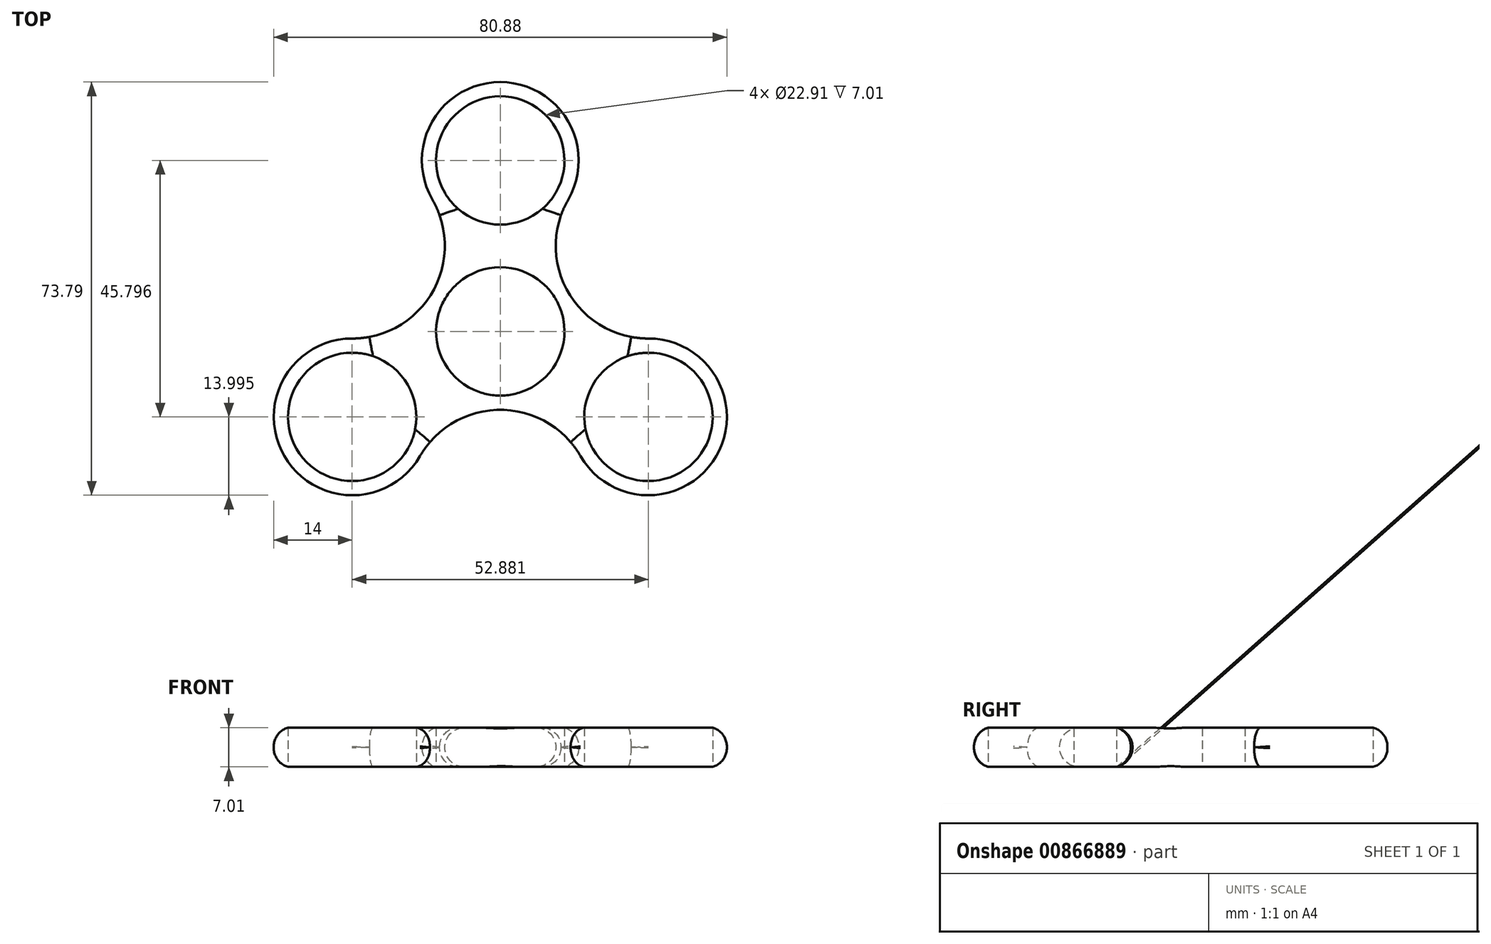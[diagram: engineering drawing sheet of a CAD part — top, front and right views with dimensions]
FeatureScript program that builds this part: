
annotation { "Feature Type Name" : "Feature", "Feature Type Description" : "" }
export const myFeature = defineFeature(function(context is Context, id is Id, definition is map)
    precondition{}
    {
        {
            var Q0;
            Q0=qCreatedBy(makeId("Top.planeOp"),FACE);
            var sketch = newSketch(context, id + "F0", { "sketchPlane" : qUnion([Q0])});
            skCircle(sketch, "E0", {"center": v(0, 0) * mm, "radius": 11.46 * mm});
            skCircle(sketch, "E1", {"center": v(0, 0) * mm, "radius": 14 * mm});
            skCircle(sketch, "E2", {"center": v(0, 30.53) * mm, "radius": 11.46 * mm});
            skCircle(sketch, "E3", {"center": v(0, 30.53) * mm, "radius": 14 * mm});
            skCircle(sketch, "E4.1.0", {"center": v(-26.44, -15.27) * mm, "radius": 11.46 * mm});
            skCircle(sketch, "E4.1.1", {"center": v(-26.44, -15.27) * mm, "radius": 14 * mm});
            skCircle(sketch, "E4.2.0", {"center": v(26.44, -15.27) * mm, "radius": 11.46 * mm});
            skCircle(sketch, "E4.2.1", {"center": v(26.44, -15.27) * mm, "radius": 14 * mm});
            skCircle(sketch, "E5", {"center": v(-26.44, 15.27) * mm, "radius": 16.54 * mm});
            skCircle(sketch, "E6.1.0", {"center": v(0, -30.53) * mm, "radius": 16.54 * mm});
            skCircle(sketch, "E6.2.0", {"center": v(26.44, 15.27) * mm, "radius": 16.54 * mm});
            skSolve(sketch);
        }
        {
            var Q0;
            Q0=makeQuery(id+"F0.imprint","IMPRINT",FACE,{"disambiguationData":[TD([[makeQuery(id+"F0.imprint","IMPRINT",EDGE,{"derivedFrom":sQuery(id+"F0.wireOp",EDGE,"E2")}),-1.0]])]});
            var Q1;
            Q1=makeQuery(id+"F0.imprint","IMPRINT",FACE,{"disambiguationData":[TD([[makeQuery(id+"F0.imprint","IMPRINT",EDGE,{"derivedFrom":sQuery(id+"F0.wireOp",EDGE,"E4.1.0")}),-1.0]])]});
            var Q2;
            Q2=makeQuery(id+"F0.imprint","IMPRINT",FACE,{"disambiguationData":[TD([[makeQuery(id+"F0.imprint","IMPRINT",EDGE,{"derivedFrom":sQuery(id+"F0.wireOp",EDGE,"E4.2.0")}),-1.0]])]});
            var Q3;
            {var subQ0=sQuery(id+"F0.wireOp",EDGE,"E5");var subQ1=sQuery(id+"F0.wireOp",EDGE,"E1");var subQ2=makeQuery(id+"F0.imprint","INTERSECT",VERTEX,{"derivedFrom":[subQ1,subQ0]});Q3=makeQuery(id+"F0.imprint","IMPRINT",FACE,{"disambiguationData":[TD([[makeQuery(id+"F0.imprint","IMPRINT",EDGE,{"disambiguationData":[TD([[subQ2,1.0]])],"derivedFrom":subQ1}),-1.0]])]});}
            var Q4;
            {var subQ0=sQuery(id+"F0.wireOp",EDGE,"E5");var subQ1=sQuery(id+"F0.wireOp",EDGE,"E1");var subQ2=makeQuery(id+"F0.imprint","INTERSECT",VERTEX,{"derivedFrom":[subQ1,subQ0]});Q4=makeQuery(id+"F0.imprint","IMPRINT",FACE,{"disambiguationData":[TD([[makeQuery(id+"F0.imprint","IMPRINT",EDGE,{"disambiguationData":[TD([[subQ2,-1.0]])],"derivedFrom":subQ1}),-1.0]])]});}
            var Q5;
            {var subQ0=sQuery(id+"F0.wireOp",EDGE,"E6.2.0");var subQ1=sQuery(id+"F0.wireOp",EDGE,"E1");var subQ2=makeQuery(id+"F0.imprint","INTERSECT",VERTEX,{"derivedFrom":[subQ1,subQ0]});Q5=makeQuery(id+"F0.imprint","IMPRINT",FACE,{"disambiguationData":[TD([[makeQuery(id+"F0.imprint","IMPRINT",EDGE,{"disambiguationData":[TD([[subQ2,1.0]])],"derivedFrom":subQ1}),-1.0]])]});}
            var Q6;
            Q6=makeQuery(id+"F0.imprint","IMPRINT",FACE,{"disambiguationData":[TD([[makeQuery(id+"F0.imprint","IMPRINT",EDGE,{"derivedFrom":sQuery(id+"F0.wireOp",EDGE,"E0")}),-1.0]])]});
            extrude(context, id + "F1", {"entities" : qUnion([Q0, Q1, Q2, Q3, Q4, Q5, Q6]), "depth" : 7 * mm, "offsetDistance" : 25.4 * mm});
        }
        {
            var Q0;
            Q0=makeQuery(id+"F1.opExtrude","CAP_EDGE",EDGE,{"disambiguationData":[OSD([sQuery(id+"F0.wireOp",EDGE,"E3")])],"isStart":true});
            var Q1;
            Q1=makeQuery(id+"F1.opExtrude","CAP_EDGE",EDGE,{"disambiguationData":[OSD([sQuery(id+"F0.wireOp",EDGE,"E3")])],"isStart":false});
            var Q2;
            Q2=makeQuery(id+"F1.opExtrude","CAP_EDGE",EDGE,{"disambiguationData":[OSD([sQuery(id+"F0.wireOp",EDGE,"E6.2.0")])],"isStart":true});
            var Q3;
            Q3=makeQuery(id+"F1.opExtrude","CAP_EDGE",EDGE,{"disambiguationData":[OSD([sQuery(id+"F0.wireOp",EDGE,"E6.2.0")])],"isStart":false});
            var Q4;
            Q4=makeQuery(id+"F1.opExtrude","CAP_EDGE",EDGE,{"disambiguationData":[OSD([sQuery(id+"F0.wireOp",EDGE,"E4.2.1")])],"isStart":false});
            var Q5;
            Q5=makeQuery(id+"F1.opExtrude","CAP_EDGE",EDGE,{"disambiguationData":[OSD([sQuery(id+"F0.wireOp",EDGE,"E4.2.1")])],"isStart":true});
            var Q6;
            Q6=makeQuery(id+"F1.opExtrude","CAP_EDGE",EDGE,{"disambiguationData":[OSD([sQuery(id+"F0.wireOp",EDGE,"E6.1.0")])],"isStart":true});
            var Q7;
            Q7=makeQuery(id+"F1.opExtrude","CAP_EDGE",EDGE,{"disambiguationData":[OSD([sQuery(id+"F0.wireOp",EDGE,"E6.1.0")])],"isStart":false});
            var Q8;
            Q8=makeQuery(id+"F1.opExtrude","CAP_EDGE",EDGE,{"disambiguationData":[OSD([sQuery(id+"F0.wireOp",EDGE,"E4.1.1")])],"isStart":false});
            var Q9;
            Q9=makeQuery(id+"F1.opExtrude","CAP_EDGE",EDGE,{"disambiguationData":[OSD([sQuery(id+"F0.wireOp",EDGE,"E4.1.1")])],"isStart":true});
            var Q10;
            Q10=makeQuery(id+"F1.opExtrude","CAP_EDGE",EDGE,{"disambiguationData":[OSD([sQuery(id+"F0.wireOp",EDGE,"E5")])],"isStart":true});
            var Q11;
            Q11=makeQuery(id+"F1.opExtrude","CAP_EDGE",EDGE,{"disambiguationData":[OSD([sQuery(id+"F0.wireOp",EDGE,"E5")])],"isStart":false});
            fillet(context, id + "F2", {"entities" : qUnion([Q0, Q1, Q2, Q3, Q4, Q5, Q6, Q7, Q8, Q9, Q10, Q11]), "radius" : 3.5 * mm, "tangentPropagation" : true, "allowEdgeOverflow" : false});
        }
    });
